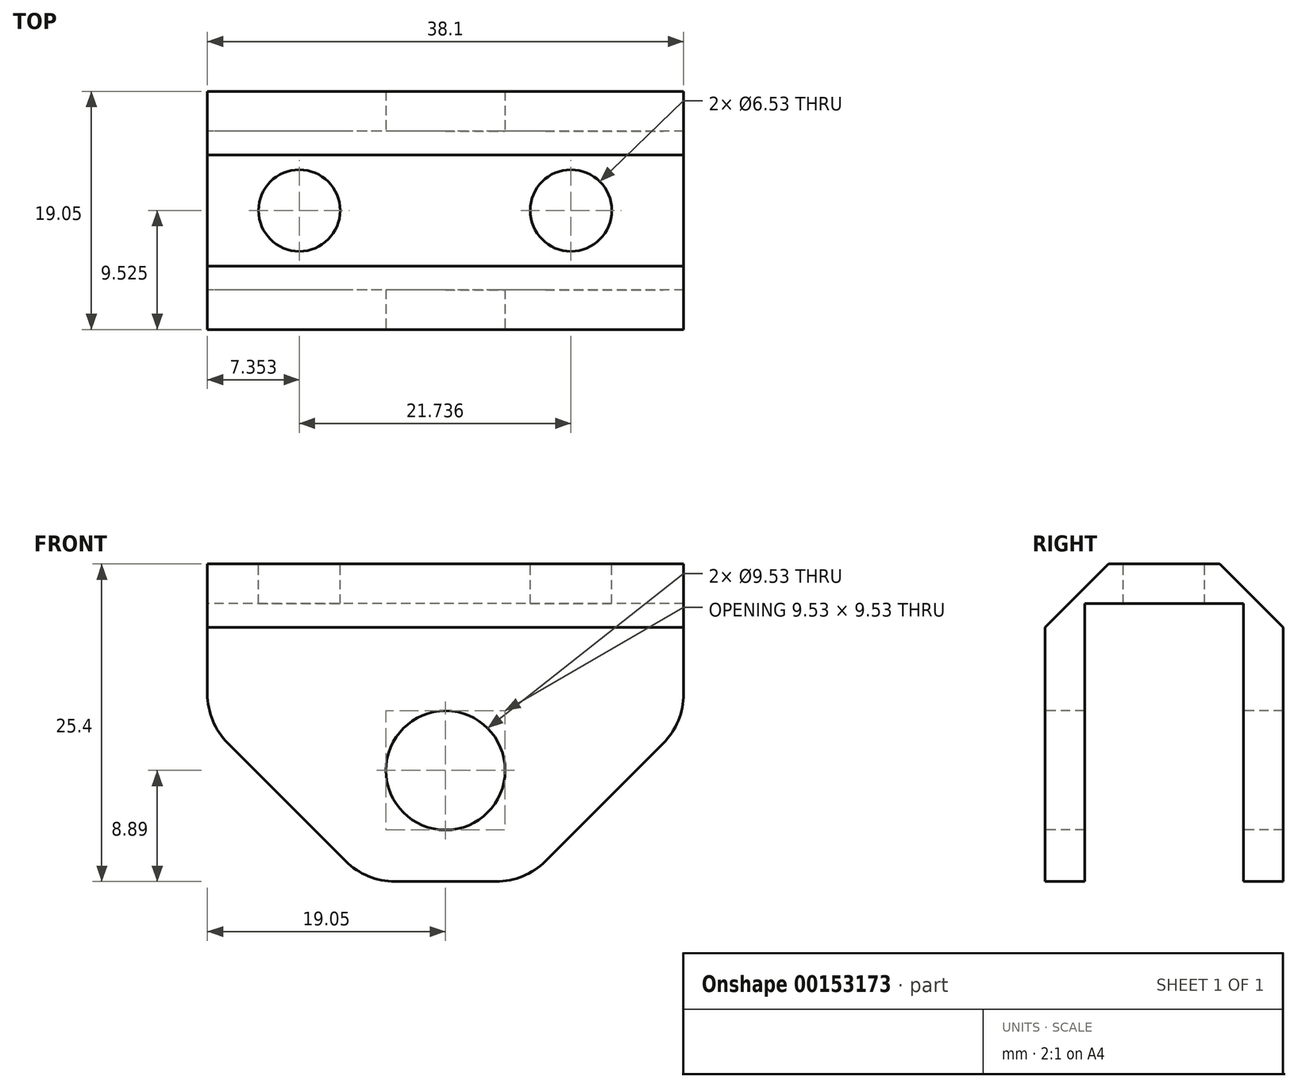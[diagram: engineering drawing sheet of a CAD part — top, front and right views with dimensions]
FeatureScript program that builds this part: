
annotation { "Feature Type Name" : "Feature", "Feature Type Description" : "" }
export const myFeature = defineFeature(function(context is Context, id is Id, definition is map)
    precondition{}
    {
        {
            var Q0;
            Q0=qCreatedBy(makeId("Top.planeOp"),FACE);
            var sketch = newSketch(context, id + "F0", { "sketchPlane" : qUnion([Q0])});
            skLineSegment(sketch, "E0.bottom", {"start": v(0, 0) * mm, "end": v(38.1, 0) * mm});
            skLineSegment(sketch, "E0.top", {"start": v(0, 19.05) * mm, "end": v(38.1, 19.05) * mm});
            skLineSegment(sketch, "E0.left", {"start": v(0, 0) * mm, "end": v(0, 19.05) * mm});
            skLineSegment(sketch, "E0.right", {"start": v(38.1, 0) * mm, "end": v(38.1, 19.05) * mm});
            skSolve(sketch);
        }
        {
            var Q0;
            Q0 = qSketchRegion(id + "F0", true);
            extrude(context, id + "F1", {"entities" : qUnion([Q0]), "oppositeDirection" : true, "depth" : 25.4 * mm});
        }
        {
            var Q0;
            Q0=makeQuery(id+"F1.opExtrude","CAP_FACE",FACE,{"disambiguationData":[OSD([sQuery(id+"F0.wireOp",EDGE,"E0.bottom"),sQuery(id+"F0.wireOp",EDGE,"E0.top"),sQuery(id+"F0.wireOp",EDGE,"E0.left"),sQuery(id+"F0.wireOp",EDGE,"E0.right")])],"isStart":true});
            var sketch = newSketch(context, id + "F2", { "sketchPlane" : qUnion([Q0])});
            skCircle(sketch, "E1", {"center": v(7.35, 9.53) * mm, "radius": 3.26 * mm});
            skCircle(sketch, "E2", {"center": v(29.09, 9.53) * mm, "radius": 3.26 * mm});
            skSolve(sketch);
        }
        {
            var Q0;
            Q0 = qSketchRegion(id + "F2", true);
            extrude(context, id + "F3", {"entities" : qUnion([Q0]), "operationType" : NewBodyOperationType.REMOVE, "oppositeDirection" : true, "depth" : 25.4 * mm});
        }
        {
            var Q0;
            Q0=makeQuery(id+"F1.opExtrude","SWEPT_FACE",FACE,{"disambiguationData":[OSD([sQuery(id+"F0.wireOp",EDGE,"E0.bottom")])]});
            var sketch = newSketch(context, id + "F4", { "sketchPlane" : qUnion([Q0])});
            skCircle(sketch, "E3", {"center": v(19.05, -16.51) * mm, "radius": 4.76 * mm});
            skSolve(sketch);
        }
        {
            var Q0;
            Q0 = qSketchRegion(id + "F4", true);
            extrude(context, id + "F5", {"entities" : qUnion([Q0]), "operationType" : NewBodyOperationType.REMOVE, "oppositeDirection" : true, "depth" : 25.4 * mm});
        }
        {
            var Q0;
            Q0=makeQuery(id+"F1.opExtrude","CAP_EDGE",EDGE,{"disambiguationData":[OSD([sQuery(id+"F0.wireOp",EDGE,"E0.right")])],"isStart":false});
            var Q1;
            Q1=makeQuery(id+"F1.opExtrude","CAP_EDGE",EDGE,{"disambiguationData":[OSD([sQuery(id+"F0.wireOp",EDGE,"E0.left")])],"isStart":false});
            chamfer(context, id + "F6", {"entities" : qUnion([Q0, Q1]), "width" : 12.7 * mm, "tangentPropagation" : true});
        }
        {
            var Q0;
            Q0=qCreatedBy(makeId("Right.planeOp"),FACE);
            var sketch = newSketch(context, id + "F7", { "sketchPlane" : qUnion([Q0])});
            skLineSegment(sketch, "E4.bottom", {"start": v(15.87, -3.17) * mm, "end": v(3.17, -3.18) * mm});
            skLineSegment(sketch, "E4.top", {"start": v(15.87, -25.4) * mm, "end": v(3.18, -25.4) * mm});
            skLineSegment(sketch, "E4.left", {"start": v(15.87, -3.18) * mm, "end": v(15.87, -25.4) * mm});
            skLineSegment(sketch, "E4.right", {"start": v(3.17, -3.18) * mm, "end": v(3.18, -25.4) * mm});
            skSolve(sketch);
        }
        {
            var Q0;
            Q0 = qSketchRegion(id + "F7", true);
            extrude(context, id + "F8", {"entities" : qUnion([Q0]), "operationType" : NewBodyOperationType.REMOVE, "depth" : 38.1 * mm});
        }
        {
            var Q0;
            {var subQ0=sQuery(id+"F0.wireOp",EDGE,"E0.left");var subQ1=makeQuery(id+"F1.opExtrude","SWEPT_FACE",FACE,{"disambiguationData":[OSD([subQ0])]});Q0=makeQuery(id+"F8.boolean.opBoolean","SPLIT",EDGE,{"disambiguationData":[TD([makeQuery(id+"F1.opExtrude","SWEPT_FACE",FACE,{"disambiguationData":[OSD([sQuery(id+"F0.wireOp",EDGE,"E0.top")])]})])],"derivedFrom":makeQuery(id+"F6.opChamfer","BLEND_EDGE",EDGE,{"blendedFrom":[makeQuery(id+"F1.opExtrude","CAP_EDGE",EDGE,{"disambiguationData":[OSD([subQ0])],"isStart":false}),subQ1],"blendedInto":[subQ1]})});}
            var Q1;
            {var subQ0=sQuery(id+"F0.wireOp",EDGE,"E0.left");var subQ1=makeQuery(id+"F1.opExtrude","SWEPT_FACE",FACE,{"disambiguationData":[OSD([subQ0])]});Q1=makeQuery(id+"F8.boolean.opBoolean","SPLIT",EDGE,{"disambiguationData":[TD([makeQuery(id+"F1.opExtrude","SWEPT_FACE",FACE,{"disambiguationData":[OSD([sQuery(id+"F0.wireOp",EDGE,"E0.bottom")])]})])],"derivedFrom":makeQuery(id+"F6.opChamfer","BLEND_EDGE",EDGE,{"blendedFrom":[makeQuery(id+"F1.opExtrude","CAP_EDGE",EDGE,{"disambiguationData":[OSD([subQ0])],"isStart":false}),subQ1],"blendedInto":[subQ1]})});}
            var Q2;
            {var subQ0=sQuery(id+"F0.wireOp",EDGE,"E0.left");var subQ1=sQuery(id+"F0.wireOp",EDGE,"E0.top");var subQ2=makeQuery(id+"F1.opExtrude","CAP_FACE",FACE,{"disambiguationData":[OSD([sQuery(id+"F0.wireOp",EDGE,"E0.bottom"),subQ1,subQ0,sQuery(id+"F0.wireOp",EDGE,"E0.right")])],"isStart":false});Q2=makeQuery(id+"F8.boolean.opBoolean","SPLIT",EDGE,{"disambiguationData":[TD([makeQuery(id+"F1.opExtrude","SWEPT_FACE",FACE,{"disambiguationData":[OSD([subQ1])]})])],"derivedFrom":makeQuery(id+"F6.opChamfer","BLEND_EDGE",EDGE,{"blendedFrom":[makeQuery(id+"F1.opExtrude","CAP_EDGE",EDGE,{"disambiguationData":[OSD([subQ0])],"isStart":false}),subQ2],"blendedInto":[subQ2]})});}
            var Q3;
            {var subQ0=sQuery(id+"F0.wireOp",EDGE,"E0.bottom");var subQ1=sQuery(id+"F0.wireOp",EDGE,"E0.left");var subQ2=makeQuery(id+"F1.opExtrude","CAP_FACE",FACE,{"disambiguationData":[OSD([subQ0,sQuery(id+"F0.wireOp",EDGE,"E0.top"),subQ1,sQuery(id+"F0.wireOp",EDGE,"E0.right")])],"isStart":false});Q3=makeQuery(id+"F8.boolean.opBoolean","SPLIT",EDGE,{"disambiguationData":[TD([makeQuery(id+"F1.opExtrude","SWEPT_FACE",FACE,{"disambiguationData":[OSD([subQ0])]})])],"derivedFrom":makeQuery(id+"F6.opChamfer","BLEND_EDGE",EDGE,{"blendedFrom":[makeQuery(id+"F1.opExtrude","CAP_EDGE",EDGE,{"disambiguationData":[OSD([subQ1])],"isStart":false}),subQ2],"blendedInto":[subQ2]})});}
            var Q4;
            {var subQ0=sQuery(id+"F0.wireOp",EDGE,"E0.bottom");var subQ1=sQuery(id+"F0.wireOp",EDGE,"E0.right");var subQ2=makeQuery(id+"F1.opExtrude","CAP_FACE",FACE,{"disambiguationData":[OSD([subQ0,sQuery(id+"F0.wireOp",EDGE,"E0.top"),sQuery(id+"F0.wireOp",EDGE,"E0.left"),subQ1])],"isStart":false});Q4=makeQuery(id+"F8.boolean.opBoolean","SPLIT",EDGE,{"disambiguationData":[TD([makeQuery(id+"F1.opExtrude","SWEPT_FACE",FACE,{"disambiguationData":[OSD([subQ0])]})])],"derivedFrom":makeQuery(id+"F6.opChamfer","BLEND_EDGE",EDGE,{"blendedFrom":[makeQuery(id+"F1.opExtrude","CAP_EDGE",EDGE,{"disambiguationData":[OSD([subQ1])],"isStart":false}),subQ2],"blendedInto":[subQ2]})});}
            var Q5;
            {var subQ0=sQuery(id+"F0.wireOp",EDGE,"E0.right");var subQ1=sQuery(id+"F0.wireOp",EDGE,"E0.top");var subQ2=makeQuery(id+"F1.opExtrude","CAP_FACE",FACE,{"disambiguationData":[OSD([sQuery(id+"F0.wireOp",EDGE,"E0.bottom"),subQ1,sQuery(id+"F0.wireOp",EDGE,"E0.left"),subQ0])],"isStart":false});Q5=makeQuery(id+"F8.boolean.opBoolean","SPLIT",EDGE,{"disambiguationData":[TD([makeQuery(id+"F1.opExtrude","SWEPT_FACE",FACE,{"disambiguationData":[OSD([subQ1])]})])],"derivedFrom":makeQuery(id+"F6.opChamfer","BLEND_EDGE",EDGE,{"blendedFrom":[makeQuery(id+"F1.opExtrude","CAP_EDGE",EDGE,{"disambiguationData":[OSD([subQ0])],"isStart":false}),subQ2],"blendedInto":[subQ2]})});}
            var Q6;
            {var subQ0=sQuery(id+"F0.wireOp",EDGE,"E0.right");var subQ1=makeQuery(id+"F1.opExtrude","SWEPT_FACE",FACE,{"disambiguationData":[OSD([subQ0])]});Q6=makeQuery(id+"F8.boolean.opBoolean","SPLIT",EDGE,{"disambiguationData":[TD([makeQuery(id+"F1.opExtrude","SWEPT_FACE",FACE,{"disambiguationData":[OSD([sQuery(id+"F0.wireOp",EDGE,"E0.top")])]})])],"derivedFrom":makeQuery(id+"F6.opChamfer","BLEND_EDGE",EDGE,{"blendedFrom":[makeQuery(id+"F1.opExtrude","CAP_EDGE",EDGE,{"disambiguationData":[OSD([subQ0])],"isStart":false}),subQ1],"blendedInto":[subQ1]})});}
            var Q7;
            {var subQ0=sQuery(id+"F0.wireOp",EDGE,"E0.right");var subQ1=makeQuery(id+"F1.opExtrude","SWEPT_FACE",FACE,{"disambiguationData":[OSD([subQ0])]});Q7=makeQuery(id+"F8.boolean.opBoolean","SPLIT",EDGE,{"disambiguationData":[TD([makeQuery(id+"F1.opExtrude","SWEPT_FACE",FACE,{"disambiguationData":[OSD([sQuery(id+"F0.wireOp",EDGE,"E0.bottom")])]})])],"derivedFrom":makeQuery(id+"F6.opChamfer","BLEND_EDGE",EDGE,{"blendedFrom":[makeQuery(id+"F1.opExtrude","CAP_EDGE",EDGE,{"disambiguationData":[OSD([subQ0])],"isStart":false}),subQ1],"blendedInto":[subQ1]})});}
            fillet(context, id + "F9", {"entities" : qUnion([Q0, Q1, Q2, Q3, Q4, Q5, Q6, Q7]), "radius" : 5.6 * mm, "tangentPropagation" : true, "allowEdgeOverflow" : false});
        }
        {
            var Q0;
            Q0=makeQuery(id+"F1.opExtrude","CAP_EDGE",EDGE,{"disambiguationData":[OSD([sQuery(id+"F0.wireOp",EDGE,"E0.top")])],"isStart":true});
            var Q1;
            Q1=makeQuery(id+"F1.opExtrude","CAP_EDGE",EDGE,{"disambiguationData":[OSD([sQuery(id+"F0.wireOp",EDGE,"E0.bottom")])],"isStart":true});
            chamfer(context, id + "F10", {"entities" : qUnion([Q0, Q1]), "width" : 5.08 * mm, "tangentPropagation" : true});
        }
    });
